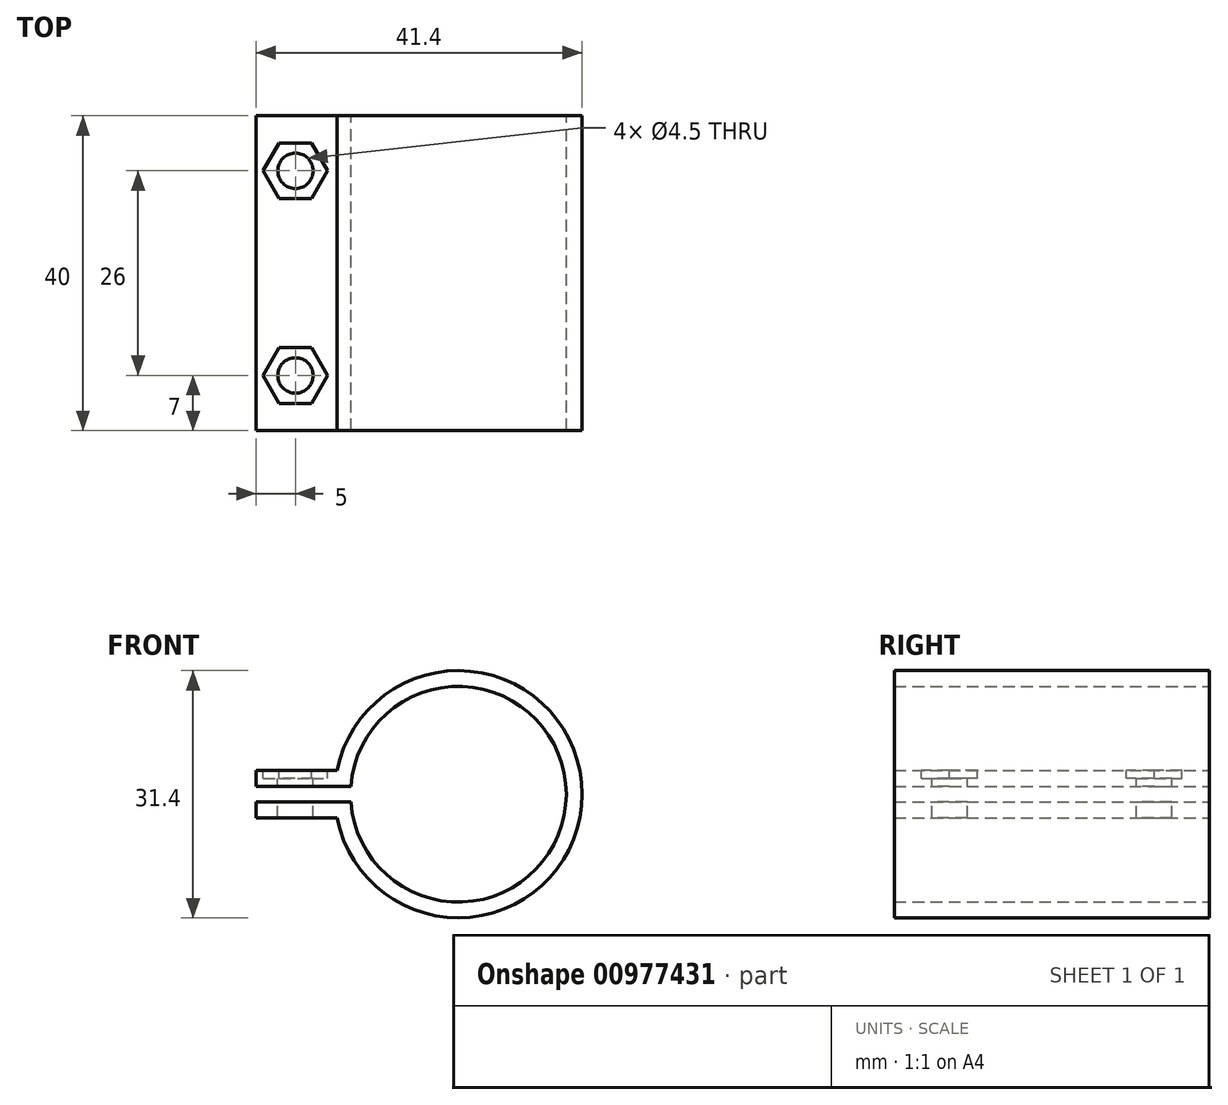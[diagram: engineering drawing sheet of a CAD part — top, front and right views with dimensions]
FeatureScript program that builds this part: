
annotation { "Feature Type Name" : "Feature", "Feature Type Description" : "" }
export const myFeature = defineFeature(function(context is Context, id is Id, definition is map)
    precondition{}
    {
        {
            var Q0;
            Q0=qCreatedBy(makeId("Front.planeOp"),FACE);
            var sketch = newSketch(context, id + "F0", { "sketchPlane" : qUnion([Q0])});
            skArc(sketch, "E0", {"start": v(-13.66, -1) * mm, "mid": v(13.7, 0) * mm, "end": v(-13.66, 1) * mm});
            skArc(sketch, "E1.0", {"start": v(-15.41, -3) * mm, "mid": v(15.7, 0) * mm, "end": v(-15.41, 3) * mm});
            skLineSegment(sketch, "E2.bottom", {"start": v(-25.7, 3) * mm, "end": v(-15.41, 3) * mm});
            skLineSegment(sketch, "E2.top", {"start": v(-25.7, -3) * mm, "end": v(-15.41, -3) * mm});
            skLineSegment(sketch, "E2.left", {"start": v(-25.7, 3) * mm, "end": v(-25.7, 1) * mm});
            skLineSegment(sketch, "E3", {"start": v(-13.66, 1) * mm, "end": v(-25.7, 1) * mm});
            skLineSegment(sketch, "E4", {"start": v(-25.7, -1) * mm, "end": v(-13.66, -1) * mm});
            skPoint(sketch, "E5.orphan", {"position": v(-24.01, 1) * mm});
            skPoint(sketch, "E6.orphan", {"position": v(-24.01, -1) * mm});
            skLineSegment(sketch, "E7.trimOffspring", {"start": v(-25.7, -1) * mm, "end": v(-25.7, -3) * mm});
            skSolve(sketch);
        }
        {
            var Q0;
            Q0 = qSketchRegion(id + "F0", true);
            extrude(context, id + "F1", {"entities" : qUnion([Q0]), "depth" : 40 * mm, "offsetDistance" : 25 * mm});
        }
        {
            var Q0;
            Q0=makeQuery(id+"F1.opExtrude","SWEPT_FACE",FACE,{"disambiguationData":[OSD([sQuery(id+"F0.wireOp",EDGE,"E2.bottom")])]});
            var sketch = newSketch(context, id + "F2", { "sketchPlane" : qUnion([Q0])});
            skCircle(sketch, "E8.cCircle", {"center": v(-20.7, -33) * mm, "radius": 3.55 * mm, "construction": true});
            skLineSegment(sketch, "E8.0", {"start": v(-18.65, -29.45) * mm, "end": v(-16.6, -33) * mm});
            skLineSegment(sketch, "E8.1", {"start": v(-16.6, -33) * mm, "end": v(-18.65, -36.55) * mm});
            skLineSegment(sketch, "E8.2", {"start": v(-18.65, -36.55) * mm, "end": v(-22.75, -36.55) * mm});
            skLineSegment(sketch, "E8.3", {"start": v(-22.75, -36.55) * mm, "end": v(-24.8, -33) * mm});
            skLineSegment(sketch, "E8.4", {"start": v(-24.8, -33) * mm, "end": v(-22.75, -29.45) * mm});
            skLineSegment(sketch, "E8.5", {"start": v(-22.75, -29.45) * mm, "end": v(-18.65, -29.45) * mm});
            skPoint(sketch, "E8.0.midPoint", {"position": v(-17.63, -31.23) * mm});
            skLineSegment(sketch, "E9", {"start": v(-36.5, -20) * mm, "end": v(-10.25, -20) * mm, "construction": true});
            skPoint(sketch, "E9.startSnap0", {"position": v(-25.7, -20) * mm});
            skCircle(sketch, "E10.MirrorC", {"center": v(-20.7, -7) * mm, "radius": 3.55 * mm, "construction": true});
            skLineSegment(sketch, "E11.MirrorCS", {"start": v(-22.75, -10.55) * mm, "end": v(-18.65, -10.55) * mm});
            skLineSegment(sketch, "E12.MirrorCS", {"start": v(-24.8, -7) * mm, "end": v(-22.75, -10.55) * mm});
            skLineSegment(sketch, "E13.MirrorCS", {"start": v(-22.75, -3.45) * mm, "end": v(-24.8, -7) * mm});
            skLineSegment(sketch, "E14.MirrorCS", {"start": v(-18.65, -3.45) * mm, "end": v(-22.75, -3.45) * mm});
            skLineSegment(sketch, "E15.MirrorCS", {"start": v(-16.6, -7) * mm, "end": v(-18.65, -3.45) * mm});
            skLineSegment(sketch, "E16.MirrorCS", {"start": v(-18.65, -10.55) * mm, "end": v(-16.6, -7) * mm});
            skSolve(sketch);
        }
        {
            var Q0;
            Q0 = qSketchRegion(id + "F2", true);
            extrude(context, id + "F3", {"entities" : qUnion([Q0]), "operationType" : NewBodyOperationType.REMOVE, "oppositeDirection" : true, "depth" : 1 * mm, "offsetDistance" : 25 * mm});
        }
        {
            var Q0;
            Q0=makeQuery(id+"F1.opExtrude","SWEPT_FACE",FACE,{"disambiguationData":[OSD([sQuery(id+"F0.wireOp",EDGE,"E2.bottom")])]});
            var sketch = newSketch(context, id + "F4", { "sketchPlane" : qUnion([Q0])});
            skLineSegment(sketch, "E17", {"start": v(-31.69, -20) * mm, "end": v(-12.48, -20) * mm, "construction": true});
            skPoint(sketch, "E17.startSnap0", {"position": v(-25.7, -20) * mm});
            skCircle(sketch, "E18", {"center": v(-20.7, -33) * mm, "radius": 2.25 * mm});
            skPoint(sketch, "E18.centerSnap0", {"position": v(-20.7, -29.45) * mm});
            skCircle(sketch, "E19.MirrorC", {"center": v(-20.7, -7) * mm, "radius": 2.25 * mm});
            skSolve(sketch);
        }
        {
            var Q0;
            Q0 = qSketchRegion(id + "F4", true);
            extrude(context, id + "F5", {"entities" : qUnion([Q0]), "operationType" : NewBodyOperationType.REMOVE, "endBound" : BoundingType.THROUGH_ALL, "oppositeDirection" : true, "depth" : 25 * mm, "offsetDistance" : 25 * mm});
        }
    });
